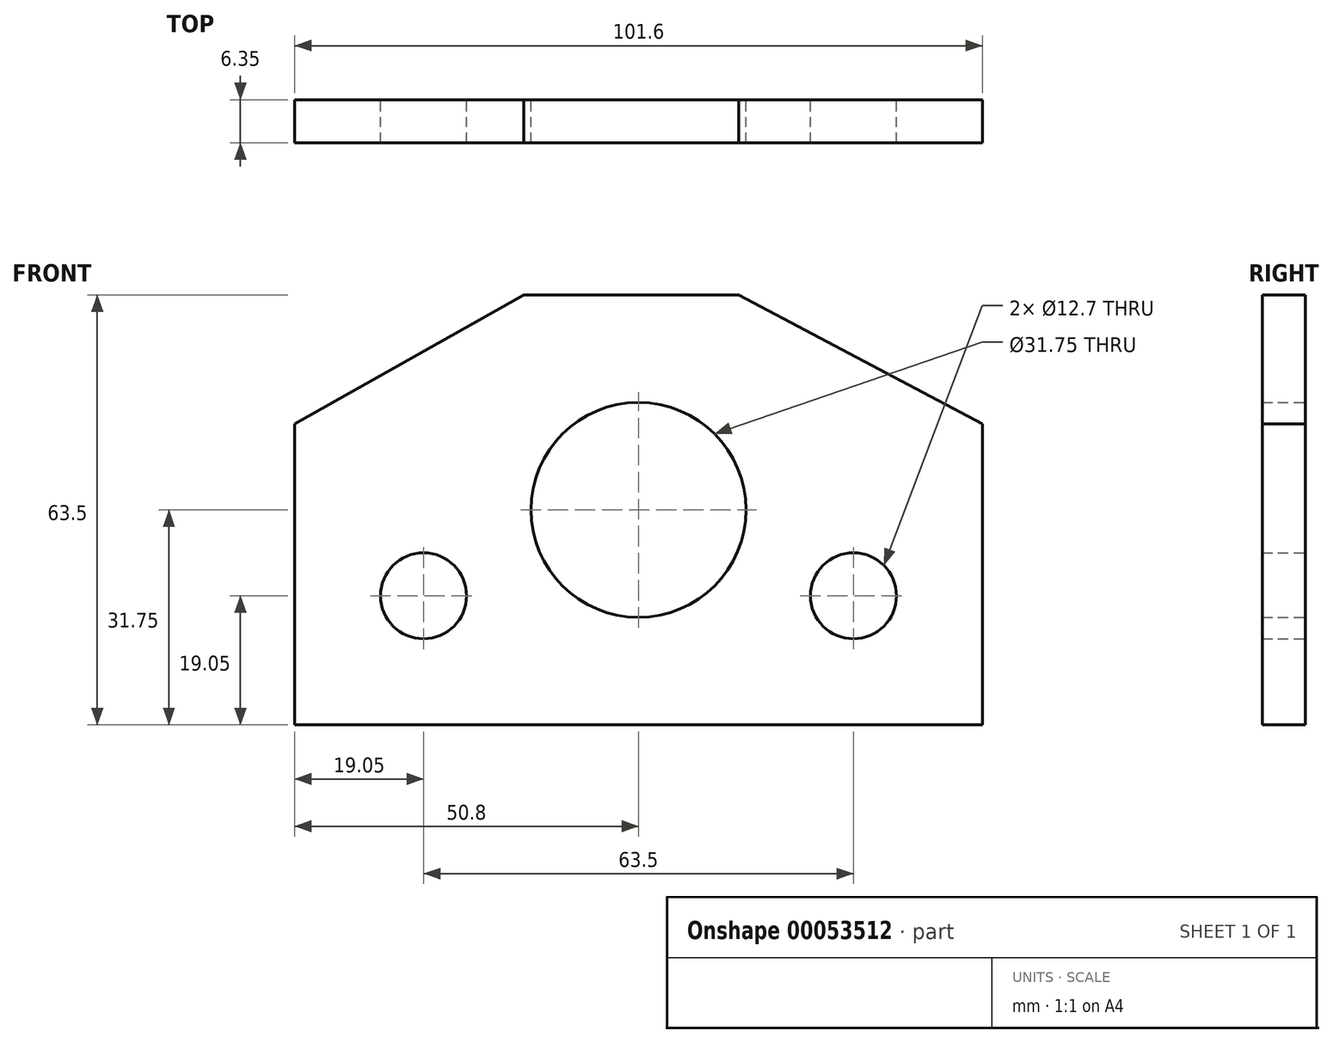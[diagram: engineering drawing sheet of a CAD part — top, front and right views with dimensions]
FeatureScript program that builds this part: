
annotation { "Feature Type Name" : "Feature", "Feature Type Description" : "" }
export const myFeature = defineFeature(function(context is Context, id is Id, definition is map)
    precondition{}
    {
        {
            var Q0;
            Q0=qCreatedBy(makeId("Front.planeOp"),FACE);
            var sketch = newSketch(context, id + "F0", { "sketchPlane" : qUnion([Q0])});
            skCircle(sketch, "E0", {"center": v(0, 0) * mm, "radius": 15.88 * mm});
            skCircle(sketch, "E1", {"center": v(-31.75, -12.7) * mm, "radius": 6.35 * mm});
            skCircle(sketch, "E2", {"center": v(31.75, -12.7) * mm, "radius": 6.35 * mm});
            skLineSegment(sketch, "E3", {"start": v(50.8, 12.7) * mm, "end": v(50.8, -31.75) * mm});
            skLineSegment(sketch, "E4", {"start": v(50.8, -31.75) * mm, "end": v(-50.8, -31.75) * mm});
            skLineSegment(sketch, "E5", {"start": v(-50.8, -31.75) * mm, "end": v(-50.8, 12.7) * mm});
            skLineSegment(sketch, "E6", {"start": v(-50.8, 12.7) * mm, "end": v(-16.95, 31.75) * mm});
            skLineSegment(sketch, "E7", {"start": v(50.8, 12.7) * mm, "end": v(14.8, 31.75) * mm});
            skLineSegment(sketch, "E8", {"start": v(14.8, 31.75) * mm, "end": v(-16.95, 31.75) * mm});
            skSolve(sketch);
        }
        {
            var Q0;
            Q0 = qSketchRegion(id + "F0", true);
            extrude(context, id + "F1", {"entities" : qUnion([Q0]), "depth" : 6.35 * mm});
        }
    });
